# Revit family: SDKL LED DOCK LIGHT
name_source: partatom
category: Lighting Fixtures
units: mm (PartAtom-declared; Revit-internal decimal feet)

## family parameters
Always vertical = Yes
Cut with Voids When Loaded = No
Host = Wall
Light Source = No
Part Type = Normal
Room Calculation Point = No
Round Connector Dimension = Use Diameter
Shared = No

## types (1)
- SDKL-50-4000K-1-BKT2-YL
    Apparent Load = 63 VA
    Average life based on 104F(HRS) = 100000
    BOLT = Bolt
    Body Material = Yellow Finish
    CCT = 4000K
    CRI = 80
    Default Elevation = 0 mm  [stored 0 ft]
    Description = The SDKL dock light has rugged die-cast aluminum housing. High impact resistant with approprite
structure design. Wattage and 3000K/4000K/5000K selectable. Adjustable pole arm mount. Industrial
safety yellow finish is standard. Ideal for energy-efficient, low maintenance loading dock lighting.
    Dimming / Control Comments = Not Dimming
    Dist = 25 mm
    END CAP = End cap
    Front Mesh = Front Mesh
    GLASS = Glass
    Holder = Yellow Finish
    INITIAL INTENSITY = 5500 lm
    IP Rating = IP65
    Lamp = SDKL LED DOCK LIGHT
    Light Inside Body = Inside Body
    Manufacturer = Above All Lighting
    Model = SDKL-50-4000K-BKT2-YL
    Type Comments = SDKL LED DOCK LIGHT
    URL = https://www.abovealllighting.com
    Voltage = 277 V
    Voltage Comments = 120-277V
    WATTS = 50 W
    Wattage Comments = 50 W

note: [stored X ft] marks values corroborated as IEEE doubles in the binary element streams (Revit-internal decimal feet)

## geometry (parser evidence)
native form markers: Sweep x25
no freeform markers — native parametric forms only
